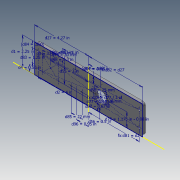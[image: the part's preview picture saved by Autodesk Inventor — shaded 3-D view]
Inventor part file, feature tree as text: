
AUTODESK INVENTOR PART (.ipt)
format: ipt  version: 2020.3 (Build 243373000, 373)  size: 175,104 bytes
history: native  units: in
note: dims shown in document units (in); Inventor stores cm internally (conversion verified against a paired STEP export)
features: hole x5, extrude x1, sketch x1, fillet x1, mirror x1
ambient origin geometry x8: Origin, YZ Plane, XZ Plane, XY Plane, X Axis, Y Axis, Z Axis, Center Point
bodies: Solid1 (feature_tree)
feature tree (9):
  extrude  "Extrusion1"  Depth=4.27in
  hole  "Hole1"  [1 undecoded]
  sketch  "Sketch3"  dims[d1=2.25in d2=4.0in d4=0.5in d5=1.2992in d8=0.23in d9=0.0in d10=0.215in d11=0.75in d12=0.375in d13=0.25in d14=0.5635in d15=1.0in d16=0.8108in d27=4.27in d44=1.1811in d45=0.093in d46=0.75in d47=0.375in d48=0.25in d49=0.5635in d50=1.0in d51=0.8108in d54=0.5689in d55=3.0in d56=0.5in d57=0.187in d58=0.9843in d59=0.7874in d62=0.093in d63=0.75in d64=0.375in d65=0.25in d66=0.5635in d67=1.0in d68=0.8108in d69=0.9in d70=0.75in d71=0.375in d72=0.25in d73=0.5635in d74=1.0in d75=0.8108in d77=1.153in d78=0.5765in d79=1.095in d80=0.3in d81=4.0in d82=4.27in d83=1.25in d84=0.5in d85=0.8661in d87=0.67in d88=0.1276in d89=0.315in d90=0.375in d91=0.25in d92=0.5635in d93=0.465in d94=0.8108in d96=0.95in d97=0.96in d98=0.3in d99=1.0in]
  hole  "Hole4 Tap M3"  [1 undecoded]
  fillet  "Fillet2"  Radius=0.23in
  hole  "Hole5"  [1 undecoded]
  hole  "Hole6"  [1 undecoded]
  hole  "Hole7 Tap M4"  [1 undecoded]
  mirror  "Mirror1"
note: 5 required parameter values undecoded (feature->parameter linkage not recoverable at this tier; creation-order binding heuristic only, values carry confidence <= 0.55)
